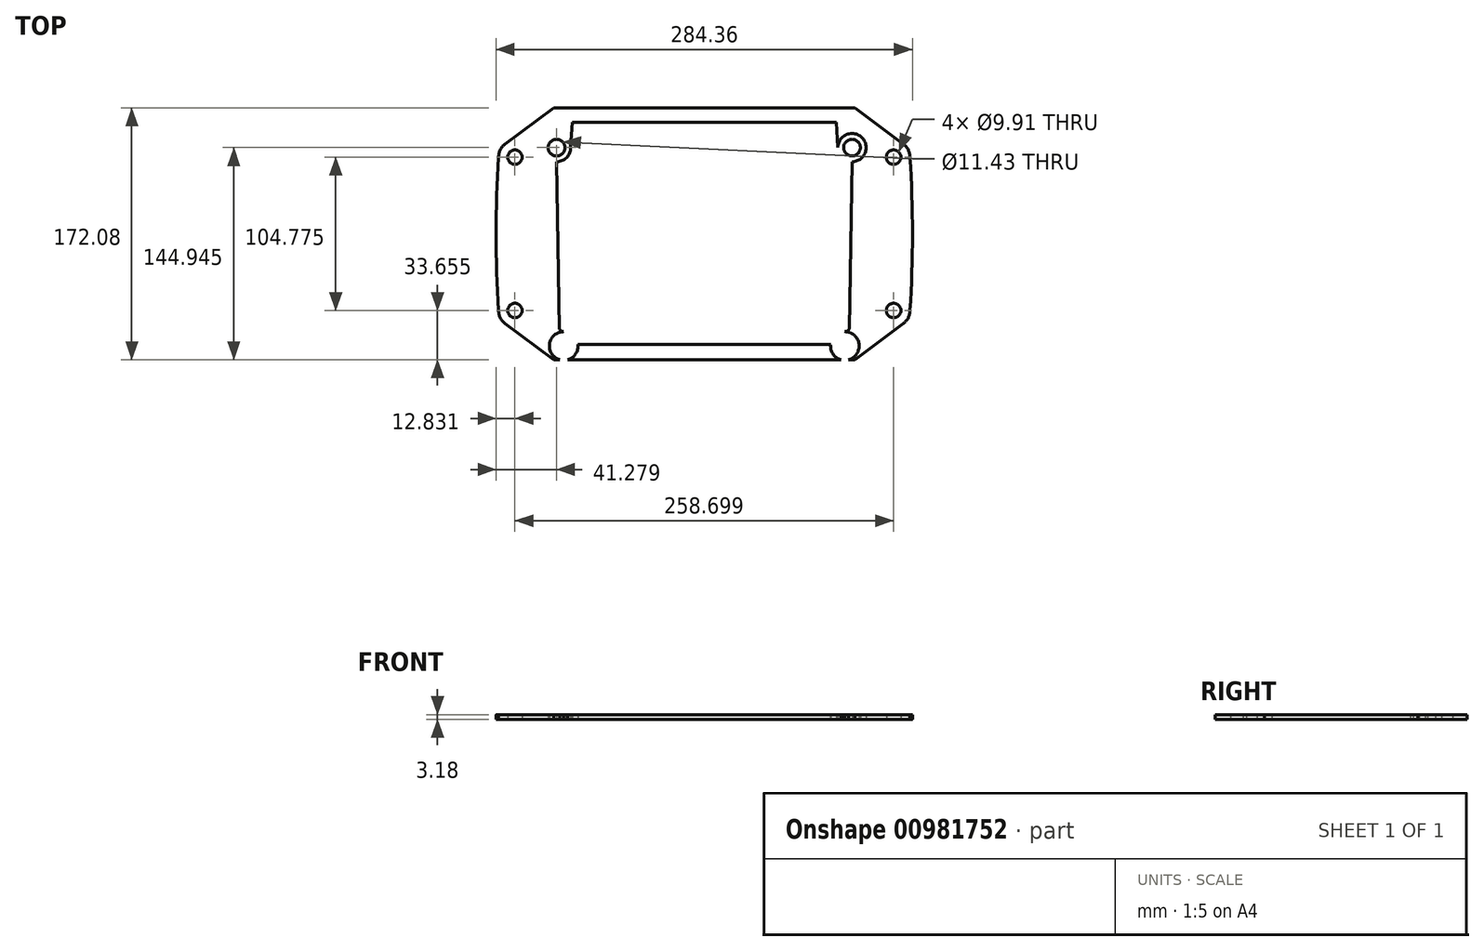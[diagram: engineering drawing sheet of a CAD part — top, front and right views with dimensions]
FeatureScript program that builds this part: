
annotation { "Feature Type Name" : "Feature", "Feature Type Description" : "" }
export const myFeature = defineFeature(function(context is Context, id is Id, definition is map)
    precondition{}
    {
        {
            var Q0;
            Q0=qCreatedBy(makeId("Top.planeOp"),FACE);
            var sketch = newSketch(context, id + "F0", { "sketchPlane" : qUnion([Q0])});
            skCircle(sketch, "E0", {"center": v(-129.35, 33.65) * mm, "radius": 4.95 * mm});
            skCircle(sketch, "E1", {"center": v(-129.35, 138.43) * mm, "radius": 4.95 * mm});
            skCircle(sketch, "E2", {"center": v(129.35, 138.43) * mm, "radius": 4.95 * mm});
            skCircle(sketch, "E3", {"center": v(129.35, 33.66) * mm, "radius": 4.95 * mm});
            skLineSegment(sketch, "E4", {"start": v(0, 0) * mm, "end": v(-142.18, 0) * mm});
            skLineSegment(sketch, "E5", {"start": v(-142.18, 0) * mm, "end": v(-142.18, 172.09) * mm});
            skLineSegment(sketch, "E6", {"start": v(-142.18, 172.09) * mm, "end": v(142.18, 172.09) * mm});
            skLineSegment(sketch, "E7", {"start": v(142.18, 172.09) * mm, "end": v(142.18, 0) * mm});
            skLineSegment(sketch, "E8", {"start": v(142.18, 0) * mm, "end": v(0, 0) * mm});
            skCircle(sketch, "E9", {"center": v(-129.35, 138.43) * mm, "radius": 11.15 * mm});
            skCircle(sketch, "E10", {"center": v(-129.35, 33.65) * mm, "radius": 11.15 * mm});
            skCircle(sketch, "E11", {"center": v(129.35, 138.43) * mm, "radius": 11.15 * mm});
            skCircle(sketch, "E12", {"center": v(129.35, 33.66) * mm, "radius": 11.15 * mm});
            skLineSegment(sketch, "E13.0", {"start": v(-142.18, 166.5) * mm, "end": v(142.18, 166.5) * mm});
            skLineSegment(sketch, "E14.0", {"start": v(0, 5.59) * mm, "end": v(-142.18, 5.59) * mm});
            skLineSegment(sketch, "E14.1", {"start": v(142.18, 5.59) * mm, "end": v(0, 5.59) * mm});
            skPoint(sketch, "E15", {"position": v(-102.87, 0) * mm});
            skLineSegment(sketch, "E16", {"start": v(-102.87, 0) * mm, "end": v(-136.02, 24.72) * mm});
            skLineSegment(sketch, "E17", {"start": v(-102.87, 172.09) * mm, "end": v(-136.02, 147.37) * mm});
            skPoint(sketch, "E18", {"position": v(-142.18, 86.04) * mm});
            skArc(sketch, "E19", {"start": v(-140.5, 138.43) * mm, "mid": v(-142.18, 86.04) * mm, "end": v(-140.5, 33.65) * mm});
            skArc(sketch, "E20.0", {"start": v(-134.16, 138.02) * mm, "mid": v(-135.83, 86.04) * mm, "end": v(-134.16, 34.06) * mm});
            skCircle(sketch, "E21", {"center": v(-96.01, 9.44) * mm, "radius": 5.72 * mm});
            skCircle(sketch, "E22", {"center": v(-100.9, 144.95) * mm, "radius": 5.72 * mm});
            skLineSegment(sketch, "E23", {"start": v(0, 0.25) * mm, "end": v(-95.59, 0.25) * mm});
            skLineSegment(sketch, "E24", {"start": v(0, 171.83) * mm, "end": v(-95.86, 171.83) * mm});
            skPoint(sketch, "E24.startSnap0", {"position": v(0, 172.09) * mm});
            skLineSegment(sketch, "E25", {"start": v(-97.63, 172.57) * mm, "end": v(-78.99, 172.57) * mm});
            skCircle(sketch, "E26", {"center": v(-96.01, 9.44) * mm, "radius": 9.78 * mm});
            skCircle(sketch, "E27", {"center": v(-100.9, 144.95) * mm, "radius": 9.65 * mm});
            skLineSegment(sketch, "E28", {"start": v(-99.06, 21.2) * mm, "end": v(-99.06, 45.55) * mm});
            skLineSegment(sketch, "E29", {"start": v(-100.9, 139.23) * mm, "end": v(-100.9, 123.35) * mm});
            skLineSegment(sketch, "E30", {"start": v(0, 10.62) * mm, "end": v(-86.3, 10.62) * mm});
            skArc(sketch, "E31", {"start": v(-99.06, 21.2) * mm, "mid": v(-97.79, 19.83) * mm, "end": v(-96.01, 19.22) * mm});
            skLineSegment(sketch, "E32", {"start": v(0, 162.18) * mm, "end": v(-90.1, 162.18) * mm});
            skLineSegment(sketch, "E33", {"start": v(-91.25, 144.95) * mm, "end": v(-90.1, 162.18) * mm});
            skLineSegment(sketch, "E34", {"start": v(-99.06, 21.2) * mm, "end": v(-100.9, 135.3) * mm});
            skLineSegment(sketch, "E35", {"start": v(0, 0) * mm, "end": v(0, -46.47) * mm});
            skLineSegment(sketch, "E36.MirrorCS", {"start": v(0, 10.62) * mm, "end": v(86.3, 10.62) * mm});
            skCircle(sketch, "E37.MirrorC", {"center": v(96.01, 9.44) * mm, "radius": 9.78 * mm});
            skCircle(sketch, "E38.MirrorC", {"center": v(96.01, 9.44) * mm, "radius": 5.72 * mm});
            skArc(sketch, "E39.MirrorCS", {"start": v(99.06, 21.2) * mm, "mid": v(97.79, 19.83) * mm, "end": v(96.01, 19.22) * mm});
            skLineSegment(sketch, "E40.MirrorCS", {"start": v(99.06, 21.2) * mm, "end": v(100.9, 135.3) * mm});
            skCircle(sketch, "E41.MirrorC", {"center": v(100.9, 144.95) * mm, "radius": 9.65 * mm});
            skCircle(sketch, "E42.MirrorC", {"center": v(100.9, 144.95) * mm, "radius": 5.72 * mm});
            skLineSegment(sketch, "E43.MirrorCS", {"start": v(91.25, 144.95) * mm, "end": v(90.1, 162.18) * mm});
            skLineSegment(sketch, "E44.MirrorCS", {"start": v(0, 162.18) * mm, "end": v(90.1, 162.18) * mm});
            skLineSegment(sketch, "E45.MirrorCS", {"start": v(102.87, 0) * mm, "end": v(136.02, 24.72) * mm});
            skLineSegment(sketch, "E46.MirrorCS", {"start": v(102.87, 172.09) * mm, "end": v(136.02, 147.37) * mm});
            skLineSegment(sketch, "E47.MirrorCS", {"start": v(142.18, 0) * mm, "end": v(142.18, 172.09) * mm});
            skArc(sketch, "E48.MirrorCS", {"start": v(140.5, 138.43) * mm, "mid": v(142.18, 86.04) * mm, "end": v(140.5, 33.65) * mm});
            skSolve(sketch);
        }
        {
            var Q0;
            {var subQ4=sQuery(id+"F0.wireOp",EDGE,"E31");Q0=makeQuery(id+"F0.imprint","IMPRINT",FACE,{"disambiguationData":[TD([[makeQuery(id+"F0.imprint","IMPRINT",EDGE,{"derivedFrom":subQ4}),-1.0]])]});}
            var Q1;
            Q1=makeQuery(id+"F0.imprint","IMPRINT",FACE,{"disambiguationData":[TD([[makeQuery(id+"F0.imprint","IMPRINT",EDGE,{"derivedFrom":sQuery(id+"F0.wireOp",EDGE,"E1")}),-1.0]])]});
            var Q2;
            {var subQ0=sQuery(id+"F0.wireOp",EDGE,"E19");var subQ4=sQuery(id+"F0.wireOp",EDGE,"E9");var subQ5=makeQuery(id+"F0.imprint","INTERSECT",VERTEX,{"derivedFrom":[subQ4,subQ0]});Q2=makeQuery(id+"F0.imprint","IMPRINT",FACE,{"disambiguationData":[TD([[makeQuery(id+"F0.imprint","IMPRINT",EDGE,{"disambiguationData":[TD([[subQ5,-1.0]])],"derivedFrom":subQ4}),-1.0]])]});}
            var Q3;
            Q3=makeQuery(id+"F0.imprint","IMPRINT",FACE,{"disambiguationData":[TD([[makeQuery(id+"F0.imprint","IMPRINT",EDGE,{"derivedFrom":sQuery(id+"F0.wireOp",EDGE,"E0")}),-1.0]])]});
            var Q4;
            {var subQ4=sQuery(id+"F0.wireOp",EDGE,"E16");var subQ5=sQuery(id+"F0.wireOp",EDGE,"E4");var subQ6=makeQuery(id+"F0.imprint","INTERSECT",VERTEX,{"derivedFrom":[subQ5,subQ4]});Q4=makeQuery(id+"F0.imprint","IMPRINT",FACE,{"disambiguationData":[TD([[makeQuery(id+"F0.imprint","IMPRINT",EDGE,{"disambiguationData":[TD([[subQ6,1.0]])],"derivedFrom":subQ5}),-1.0]])]});}
            var Q5;
            {var subQ0=sQuery(id+"F0.wireOp",EDGE,"E26");var subQ5=sQuery(id+"F0.wireOp",EDGE,"E14.0");var subQ9=makeQuery(id+"F0.imprint","INTERSECT",VERTEX,{"disambiguationData":[OD(0.0)],"derivedFrom":[subQ5,subQ0]});Q5=makeQuery(id+"F0.imprint","IMPRINT",FACE,{"disambiguationData":[TD([[makeQuery(id+"F0.imprint","IMPRINT",EDGE,{"disambiguationData":[TD([[subQ9,-1.0]])],"derivedFrom":subQ5}),1.0]])]});}
            var Q6;
            {var subQ1=sQuery(id+"F0.wireOp",EDGE,"E14.0");var subQ4=sQuery(id+"F0.wireOp",EDGE,"E26");var subQ7=makeQuery(id+"F0.imprint","INTERSECT",VERTEX,{"disambiguationData":[OD(0.0)],"derivedFrom":[subQ1,subQ4]});Q6=makeQuery(id+"F0.imprint","IMPRINT",FACE,{"disambiguationData":[TD([[makeQuery(id+"F0.imprint","IMPRINT",EDGE,{"disambiguationData":[TD([[subQ7,-1.0]])],"derivedFrom":subQ1}),-1.0]])]});}
            var Q7;
            {var subQ7=sQuery(id+"F0.wireOp",EDGE,"E8");var subQ8=sQuery(id+"F0.wireOp",EDGE,"E4");var subQ9=makeQuery(id+"F0.imprint","INTERSECT",VERTEX,{"derivedFrom":[subQ8,subQ7]});Q7=makeQuery(id+"F0.imprint","IMPRINT",FACE,{"disambiguationData":[TD([[makeQuery(id+"F0.imprint","IMPRINT",EDGE,{"disambiguationData":[TD([[subQ9,-1.0]])],"derivedFrom":subQ8}),-1.0]])]});}
            var Q8;
            {var subQ0=sQuery(id+"F0.wireOp",EDGE,"E30");Q8=makeQuery(id+"F0.imprint","IMPRINT",FACE,{"disambiguationData":[TD([[makeQuery(id+"F0.imprint","IMPRINT",EDGE,{"derivedFrom":subQ0}),1.0]])]});}
            var Q9;
            {var subQ0=sQuery(id+"F0.wireOp",EDGE,"E37.MirrorC");var subQ1=sQuery(id+"F0.wireOp",EDGE,"E8");var subQ2=makeQuery(id+"F0.imprint","INTERSECT",VERTEX,{"disambiguationData":[OD(0.0)],"derivedFrom":[subQ1,subQ0]});Q9=makeQuery(id+"F0.imprint","IMPRINT",FACE,{"disambiguationData":[TD([[makeQuery(id+"F0.imprint","IMPRINT",EDGE,{"disambiguationData":[TD([[subQ2,-1.0]])],"derivedFrom":subQ1}),-1.0]])]});}
            var Q10;
            {var subQ0=sQuery(id+"F0.wireOp",EDGE,"E37.MirrorC");var subQ3=sQuery(id+"F0.wireOp",EDGE,"E14.1");var subQ4=makeQuery(id+"F0.imprint","INTERSECT",VERTEX,{"disambiguationData":[OD(0.0)],"derivedFrom":[subQ3,subQ0]});Q10=makeQuery(id+"F0.imprint","IMPRINT",FACE,{"disambiguationData":[TD([[makeQuery(id+"F0.imprint","IMPRINT",EDGE,{"disambiguationData":[TD([[subQ4,-1.0]])],"derivedFrom":subQ3}),-1.0]])]});}
            var Q11;
            {var subQ0=sQuery(id+"F0.wireOp",EDGE,"E45.MirrorCS");var subQ1=sQuery(id+"F0.wireOp",EDGE,"E8");var subQ2=makeQuery(id+"F0.imprint","INTERSECT",VERTEX,{"derivedFrom":[subQ1,subQ0]});Q11=makeQuery(id+"F0.imprint","IMPRINT",FACE,{"disambiguationData":[TD([[makeQuery(id+"F0.imprint","IMPRINT",EDGE,{"disambiguationData":[TD([[subQ2,-1.0]])],"derivedFrom":subQ1}),-1.0]])]});}
            var Q12;
            Q12=makeQuery(id+"F0.imprint","IMPRINT",FACE,{"disambiguationData":[TD([[makeQuery(id+"F0.imprint","IMPRINT",EDGE,{"derivedFrom":sQuery(id+"F0.wireOp",EDGE,"E3")}),-1.0]])]});
            var Q13;
            Q13=makeQuery(id+"F0.imprint","IMPRINT",FACE,{"disambiguationData":[TD([[makeQuery(id+"F0.imprint","IMPRINT",EDGE,{"derivedFrom":sQuery(id+"F0.wireOp",EDGE,"E2")}),-1.0]])]});
            var Q14;
            Q14=makeQuery(id+"F0.imprint","IMPRINT",FACE,{"disambiguationData":[TD([[makeQuery(id+"F0.imprint","IMPRINT",EDGE,{"derivedFrom":sQuery(id+"F0.wireOp",EDGE,"E42.MirrorC")}),1.0]])]});
            var Q15;
            {var subQ0=sQuery(id+"F0.wireOp",EDGE,"E17");var subQ1=sQuery(id+"F0.wireOp",EDGE,"E6");var subQ2=makeQuery(id+"F0.imprint","INTERSECT",VERTEX,{"derivedFrom":[subQ1,subQ0]});Q15=makeQuery(id+"F0.imprint","IMPRINT",FACE,{"disambiguationData":[TD([[makeQuery(id+"F0.imprint","IMPRINT",EDGE,{"disambiguationData":[TD([[subQ2,-1.0]])],"derivedFrom":subQ1}),-1.0]])]});}
            var Q16;
            Q16=makeQuery(id+"F0.imprint","IMPRINT",FACE,{"disambiguationData":[TD([[makeQuery(id+"F0.imprint","IMPRINT",EDGE,{"derivedFrom":sQuery(id+"F0.wireOp",EDGE,"E22")}),-1.0]])]});
            extrude(context, id + "F1", {"entities" : qUnion([Q0, Q1, Q2, Q3, Q4, Q5, Q6, Q7, Q8, Q9, Q10, Q11, Q12, Q13, Q14, Q15, Q16]), "depth" : 3.17 * mm, "offsetDistance" : 25.4 * mm});
        }
    });
